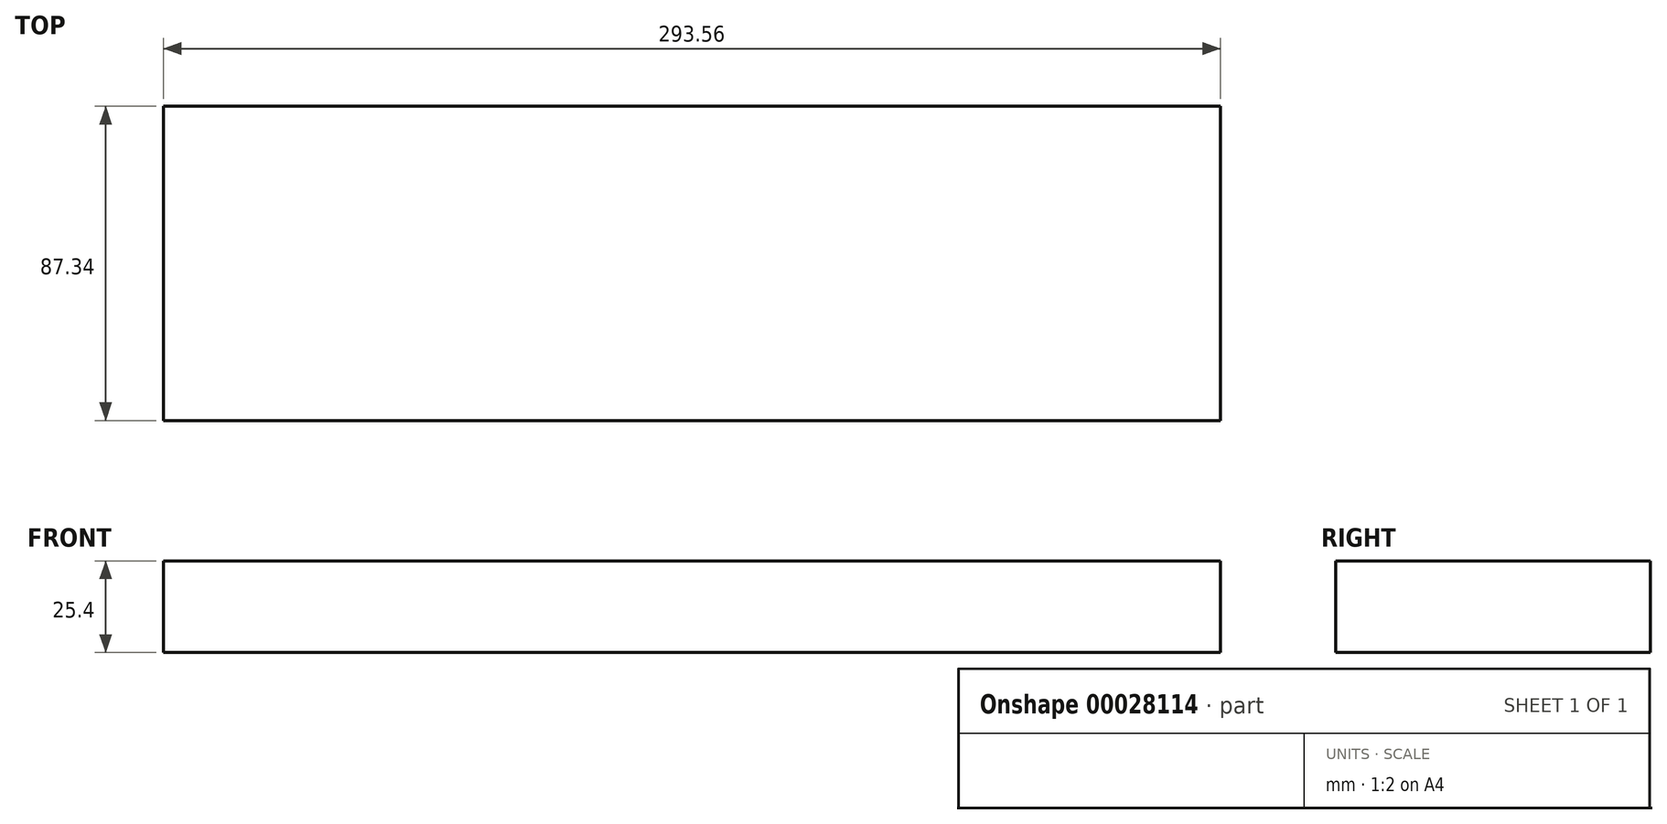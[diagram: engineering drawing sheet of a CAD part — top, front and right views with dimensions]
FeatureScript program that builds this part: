
annotation { "Feature Type Name" : "Feature", "Feature Type Description" : "" }
export const myFeature = defineFeature(function(context is Context, id is Id, definition is map)
    precondition{}
    {
        {
            var Q0;
            Q0=qCreatedBy(makeId("Top.planeOp"),FACE);
            var sketch = newSketch(context, id + "F0", { "sketchPlane" : qUnion([Q0])});
            skLineSegment(sketch, "E0.bottom", {"start": v(-145.8, -23.86) * mm, "end": v(147.75, -23.86) * mm});
            skLineSegment(sketch, "E0.top", {"start": v(-145.8, 63.48) * mm, "end": v(147.75, 63.48) * mm});
            skLineSegment(sketch, "E0.left", {"start": v(-145.8, -23.86) * mm, "end": v(-145.8, 63.48) * mm});
            skLineSegment(sketch, "E0.right", {"start": v(147.75, -23.86) * mm, "end": v(147.75, 63.48) * mm});
            skSolve(sketch);
        }
        {
            var Q0;
            Q0 = qSketchRegion(id + "F0", true);
            extrude(context, id + "F1", {"entities" : qUnion([Q0]), "depth" : 25.4 * mm});
        }
    });
